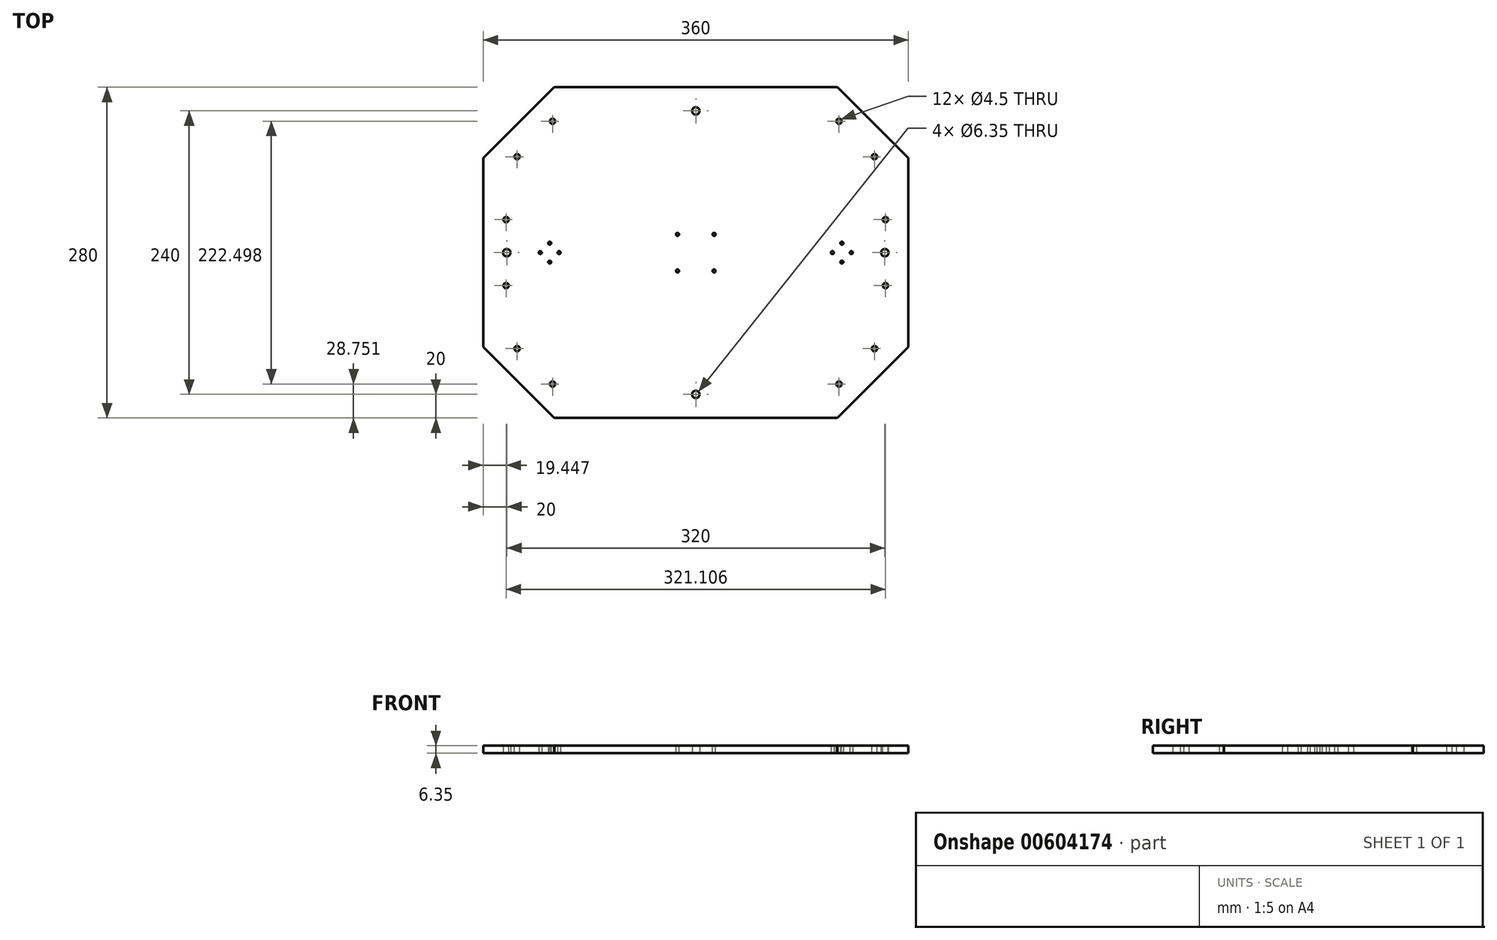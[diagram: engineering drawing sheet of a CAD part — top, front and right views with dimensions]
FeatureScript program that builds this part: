
annotation { "Feature Type Name" : "Feature", "Feature Type Description" : "" }
export const myFeature = defineFeature(function(context is Context, id is Id, definition is map)
    precondition{}
    {
        {
            var Q0;
            Q0=qCreatedBy(makeId("Top.planeOp"),FACE);
            var sketch = newSketch(context, id + "F0", { "sketchPlane" : qUnion([Q0])});
            skLineSegment(sketch, "E0", {"start": v(-120, 0) * mm, "end": v(-180, 60) * mm});
            skLineSegment(sketch, "E1", {"start": v(-180, 60) * mm, "end": v(-180, 220) * mm});
            skLineSegment(sketch, "E2", {"start": v(-180, 220) * mm, "end": v(-120, 280) * mm});
            skLineSegment(sketch, "E3", {"start": v(-120, 280) * mm, "end": v(120, 280) * mm});
            skLineSegment(sketch, "E4", {"start": v(120, 280) * mm, "end": v(180, 220) * mm});
            skLineSegment(sketch, "E5", {"start": v(180, 220) * mm, "end": v(180, 60) * mm});
            skLineSegment(sketch, "E6", {"start": v(180, 60) * mm, "end": v(120, 0) * mm});
            skLineSegment(sketch, "E7", {"start": v(120, 0) * mm, "end": v(-120, 0) * mm});
            skLineSegment(sketch, "E8", {"start": v(-180, 140) * mm, "end": v(-160, 140) * mm, "construction": true});
            skLineSegment(sketch, "E9", {"start": v(0, 280) * mm, "end": v(0, 260) * mm, "construction": true});
            skPoint(sketch, "E9.endSnap0", {"position": v(0, 280) * mm});
            skLineSegment(sketch, "E10", {"start": v(180, 140) * mm, "end": v(160, 140) * mm, "construction": true});
            skLineSegment(sketch, "E11", {"start": v(0, 0) * mm, "end": v(0, 20) * mm, "construction": true});
            skCircle(sketch, "E12", {"center": v(0, 20) * mm, "radius": 3.18 * mm});
            skCircle(sketch, "E13", {"center": v(160, 140) * mm, "radius": 3.18 * mm});
            skCircle(sketch, "E14", {"center": v(0, 260) * mm, "radius": 3.18 * mm});
            skCircle(sketch, "E15", {"center": v(-160, 140) * mm, "radius": 3.18 * mm});
            skLineSegment(sketch, "E16", {"start": v(-180, 140) * mm, "end": v(180, 140) * mm, "construction": true});
            skCircle(sketch, "E17", {"center": v(-123.65, 140) * mm, "radius": 8 * mm, "construction": true});
            skCircle(sketch, "E18", {"center": v(123.65, 140) * mm, "radius": 8 * mm, "construction": true});
            skPoint(sketch, "E19", {"position": v(-123.65, 148) * mm});
            skPoint(sketch, "E20", {"position": v(-123.65, 132) * mm});
            skPoint(sketch, "E21", {"position": v(-115.65, 140) * mm});
            skPoint(sketch, "E22", {"position": v(-131.65, 140) * mm});
            skPoint(sketch, "E23", {"position": v(131.65, 140) * mm});
            skPoint(sketch, "E24", {"position": v(115.65, 140) * mm});
            skPoint(sketch, "E25", {"position": v(123.65, 148) * mm});
            skPoint(sketch, "E26", {"position": v(123.65, 132) * mm});
            skPoint(sketch, "E27", {"position": v(0, 140) * mm});
            skSolve(sketch);
        }
        {
            var Q0;
            Q0=makeQuery(id+"F0.imprint","IMPRINT",FACE,{"disambiguationData":[TD([[makeQuery(id+"F0.imprint","IMPRINT",EDGE,{"derivedFrom":sQuery(id+"F0.wireOp",EDGE,"E0")}),-1.0]])]});
            extrude(context, id + "F1", {"entities" : qUnion([Q0]), "depth" : 6.35 * mm, "offsetDistance" : 25 * mm});
        }
        {
            var Q0;
            Q0=makeQuery(id+"F1.opExtrude","CAP_FACE",FACE,{"disambiguationData":[OSD([sQuery(id+"F0.wireOp",EDGE,"E0"),sQuery(id+"F0.wireOp",EDGE,"E1"),sQuery(id+"F0.wireOp",EDGE,"E2"),sQuery(id+"F0.wireOp",EDGE,"E3"),sQuery(id+"F0.wireOp",EDGE,"E4"),sQuery(id+"F0.wireOp",EDGE,"E5"),sQuery(id+"F0.wireOp",EDGE,"E6"),sQuery(id+"F0.wireOp",EDGE,"E7"),sQuery(id+"F0.wireOp",EDGE,"E12"),sQuery(id+"F0.wireOp",EDGE,"E13"),sQuery(id+"F0.wireOp",EDGE,"E14"),sQuery(id+"F0.wireOp",EDGE,"E15")])],"isStart":false});
            var sketch = newSketch(context, id + "F2", { "sketchPlane" : qUnion([Q0])});
            skLineSegment(sketch, "E28", {"start": v(-180, 140) * mm, "end": v(180, 140) * mm, "construction": true});
            skPoint(sketch, "E29", {"position": v(0, 140) * mm});
            skLineSegment(sketch, "E30.bottom", {"start": v(15.5, 155.5) * mm, "end": v(-15.5, 155.5) * mm, "construction": true});
            skLineSegment(sketch, "E30.top", {"start": v(15.5, 124.5) * mm, "end": v(-15.5, 124.5) * mm, "construction": true});
            skLineSegment(sketch, "E30.left", {"start": v(15.5, 155.5) * mm, "end": v(15.5, 124.5) * mm, "construction": true});
            skLineSegment(sketch, "E30.right", {"start": v(-15.5, 155.5) * mm, "end": v(-15.5, 124.5) * mm, "construction": true});
            skSolve(sketch);
        }
        {
            var Q0;
            Q0=sQuery(id+"F2.wireOp",VERTEX,"E30.bottom.end");
            var Q1;
            Q1=sQuery(id+"F2.wireOp",VERTEX,"E30.left.start");
            var Q2;
            Q2=sQuery(id+"F2.wireOp",VERTEX,"E30.top.start");
            var Q3;
            Q3=sQuery(id+"F2.wireOp",VERTEX,"E30.top.end");
            var Q4;
            Q4=makeQuery(id+"F1.opExtrude","SWEPT_BODY",BODY,{"disambiguationData":[OSD([sQuery(id+"F0.wireOp",EDGE,"E0"),sQuery(id+"F0.wireOp",EDGE,"E1"),sQuery(id+"F0.wireOp",EDGE,"E2"),sQuery(id+"F0.wireOp",EDGE,"E3"),sQuery(id+"F0.wireOp",EDGE,"E4"),sQuery(id+"F0.wireOp",EDGE,"E5"),sQuery(id+"F0.wireOp",EDGE,"E6"),sQuery(id+"F0.wireOp",EDGE,"E7"),sQuery(id+"F0.wireOp",EDGE,"E12"),sQuery(id+"F0.wireOp",EDGE,"E13"),sQuery(id+"F0.wireOp",EDGE,"E14"),sQuery(id+"F0.wireOp",EDGE,"E15")])]});
            hole(context, id + "F3", {"style" : HoleStyle.SIMPLE, "endStyle" : HoleEndStyle.BLIND, "standardTappedOrClearance" : lookupTablePath({ "standard" : "ANSI", "engagement" : "75%", "pitch" : "40 tpi", "size" : "#5", "type" : "Tapped" }), "standardBlindInLast" : lookupTablePath({ "standard" : "ANSI", "engagement" : "75%", "pitch" : "40 tpi", "size" : "#5", "type" : "Tapped" }), "holeDiameter" : 2.58 * mm, "majorDiameter" : 3.17 * mm, "showTappedDepth" : true, "holeDepth" : 13.9 * mm, "isTappedThrough" : true, "tappedDepth" : 12 * mm, "tapClearance" : 3, "locations" : qUnion([Q0, Q1, Q2, Q3]), "scope" : qUnion([Q4])});
        }
        {
            var Q0;
            Q0=makeQuery(id+"F1.opExtrude","CAP_FACE",FACE,{"disambiguationData":[OSD([sQuery(id+"F0.wireOp",EDGE,"E0"),sQuery(id+"F0.wireOp",EDGE,"E1"),sQuery(id+"F0.wireOp",EDGE,"E2"),sQuery(id+"F0.wireOp",EDGE,"E3"),sQuery(id+"F0.wireOp",EDGE,"E4"),sQuery(id+"F0.wireOp",EDGE,"E5"),sQuery(id+"F0.wireOp",EDGE,"E6"),sQuery(id+"F0.wireOp",EDGE,"E7"),sQuery(id+"F0.wireOp",EDGE,"E12"),sQuery(id+"F0.wireOp",EDGE,"E13"),sQuery(id+"F0.wireOp",EDGE,"E14"),sQuery(id+"F0.wireOp",EDGE,"E15")])],"isStart":false});
            var sketch = newSketch(context, id + "F4", { "sketchPlane" : qUnion([Q0])});
            skLineSegment(sketch, "E31", {"start": v(-180, 140) * mm, "end": v(-180, 167.94) * mm, "construction": true});
            skLineSegment(sketch, "E32", {"start": v(-180, 140) * mm, "end": v(-180, 112.06) * mm, "construction": true});
            skLineSegment(sketch, "E33", {"start": v(-180, 167.94) * mm, "end": v(-160.55, 167.94) * mm, "construction": true});
            skLineSegment(sketch, "E34", {"start": v(-180, 112.06) * mm, "end": v(-160.55, 112.06) * mm, "construction": true});
            skLineSegment(sketch, "E35", {"start": v(0, 280) * mm, "end": v(0, 0) * mm, "construction": true});
            skLineSegment(sketch, "E36.MirrorCS", {"start": v(180, 167.94) * mm, "end": v(160.55, 167.94) * mm, "construction": true});
            skLineSegment(sketch, "E37.MirrorCS", {"start": v(180, 112.06) * mm, "end": v(160.55, 112.06) * mm, "construction": true});
            skLineSegment(sketch, "E38", {"start": v(-120, 280) * mm, "end": v(-180, 220) * mm, "construction": true});
            skLineSegment(sketch, "E39", {"start": v(-180, 220) * mm, "end": v(-150, 250) * mm, "construction": true});
            skLineSegment(sketch, "E40", {"start": v(-150, 250) * mm, "end": v(-165, 235) * mm, "construction": true});
            skLineSegment(sketch, "E41", {"start": v(-165, 235) * mm, "end": v(-151.25, 221.25) * mm, "construction": true});
            skLineSegment(sketch, "E42", {"start": v(-150, 250) * mm, "end": v(-112, 212) * mm, "construction": true});
            skLineSegment(sketch, "E43.MirrorCS", {"start": v(-135, 265) * mm, "end": v(-121.25, 251.25) * mm, "construction": true});
            skLineSegment(sketch, "E44.MirrorCS", {"start": v(135, 265) * mm, "end": v(121.25, 251.25) * mm, "construction": true});
            skLineSegment(sketch, "E45.MirrorCS", {"start": v(165, 235) * mm, "end": v(151.25, 221.25) * mm, "construction": true});
            skLineSegment(sketch, "E46", {"start": v(-180, 60) * mm, "end": v(-120, 0) * mm, "construction": true});
            skLineSegment(sketch, "E47", {"start": v(-120, 0) * mm, "end": v(-150, 30) * mm, "construction": true});
            skLineSegment(sketch, "E48", {"start": v(-150, 30) * mm, "end": v(-135, 15) * mm, "construction": true});
            skLineSegment(sketch, "E49", {"start": v(-135, 15) * mm, "end": v(-121.25, 28.75) * mm, "construction": true});
            skLineSegment(sketch, "E50", {"start": v(-150, 30) * mm, "end": v(-108.05, 71.95) * mm, "construction": true});
            skLineSegment(sketch, "E51.MirrorCS", {"start": v(-165, 45) * mm, "end": v(-151.25, 58.75) * mm, "construction": true});
            skLineSegment(sketch, "E52.MirrorCS", {"start": v(165, 45) * mm, "end": v(151.25, 58.75) * mm, "construction": true});
            skLineSegment(sketch, "E53.MirrorCS", {"start": v(135, 15) * mm, "end": v(121.25, 28.75) * mm, "construction": true});
            skLineSegment(sketch, "E54", {"start": v(-151.25, 221.25) * mm, "end": v(-149.9, 222.6) * mm, "construction": true});
            skLineSegment(sketch, "E55", {"start": v(-121.25, 251.25) * mm, "end": v(-122.6, 249.9) * mm, "construction": true});
            skLineSegment(sketch, "E56", {"start": v(-121.25, 28.75) * mm, "end": v(-122.6, 30.1) * mm, "construction": true});
            skLineSegment(sketch, "E57", {"start": v(-151.25, 58.75) * mm, "end": v(-149.9, 57.4) * mm, "construction": true});
            skLineSegment(sketch, "E58.MirrorCS", {"start": v(121.25, 28.75) * mm, "end": v(122.6, 30.1) * mm, "construction": true});
            skLineSegment(sketch, "E59.MirrorCS", {"start": v(151.25, 58.75) * mm, "end": v(149.9, 57.4) * mm, "construction": true});
            skLineSegment(sketch, "E60.MirrorCS", {"start": v(151.25, 221.25) * mm, "end": v(149.9, 222.6) * mm, "construction": true});
            skLineSegment(sketch, "E61.MirrorCS", {"start": v(121.25, 251.25) * mm, "end": v(122.6, 249.9) * mm, "construction": true});
            skLineSegment(sketch, "E62", {"start": v(180, 140) * mm, "end": v(0, 140) * mm, "construction": true});
            skSolve(sketch);
        }
        {
            var Q0;
            Q0=sQuery(id+"F4.wireOp",VERTEX,"E33.end");
            var Q1;
            Q1=sQuery(id+"F4.wireOp",VERTEX,"E34.end");
            var Q2;
            Q2=sQuery(id+"F4.wireOp",VERTEX,"E37.MirrorCS.end");
            var Q3;
            Q3=sQuery(id+"F4.wireOp",VERTEX,"E36.MirrorCS.end");
            var Q4;
            Q4=makeQuery(id+"F1.opExtrude","SWEPT_BODY",BODY,{"disambiguationData":[OSD([sQuery(id+"F0.wireOp",EDGE,"E0"),sQuery(id+"F0.wireOp",EDGE,"E1"),sQuery(id+"F0.wireOp",EDGE,"E2"),sQuery(id+"F0.wireOp",EDGE,"E3"),sQuery(id+"F0.wireOp",EDGE,"E4"),sQuery(id+"F0.wireOp",EDGE,"E5"),sQuery(id+"F0.wireOp",EDGE,"E6"),sQuery(id+"F0.wireOp",EDGE,"E7"),sQuery(id+"F0.wireOp",EDGE,"E12"),sQuery(id+"F0.wireOp",EDGE,"E13"),sQuery(id+"F0.wireOp",EDGE,"E14"),sQuery(id+"F0.wireOp",EDGE,"E15")])]});
            hole(context, id + "F5", {"style" : HoleStyle.SIMPLE, "endStyle" : HoleEndStyle.THROUGH, "holeDiameter" : 4.5 * mm, "majorDiameter" : 5 * mm, "isTappedThrough" : true, "tappedDepth" : 12 * mm, "tapClearance" : 3, "locations" : qUnion([Q0, Q1, Q2, Q3]), "scope" : qUnion([Q4])});
        }
        {
            var Q0;
            Q0=sQuery(id+"F4.wireOp",VERTEX,"E54.start");
            var Q1;
            Q1=sQuery(id+"F4.wireOp",VERTEX,"E55.start");
            var Q2;
            Q2=makeQuery(id+"F1.opExtrude","SWEPT_BODY",BODY,{"disambiguationData":[OSD([sQuery(id+"F0.wireOp",EDGE,"E0"),sQuery(id+"F0.wireOp",EDGE,"E1"),sQuery(id+"F0.wireOp",EDGE,"E2"),sQuery(id+"F0.wireOp",EDGE,"E3"),sQuery(id+"F0.wireOp",EDGE,"E4"),sQuery(id+"F0.wireOp",EDGE,"E5"),sQuery(id+"F0.wireOp",EDGE,"E6"),sQuery(id+"F0.wireOp",EDGE,"E7"),sQuery(id+"F0.wireOp",EDGE,"E12"),sQuery(id+"F0.wireOp",EDGE,"E13"),sQuery(id+"F0.wireOp",EDGE,"E14"),sQuery(id+"F0.wireOp",EDGE,"E15")])]});
            hole(context, id + "F6", {"style" : HoleStyle.SIMPLE, "endStyle" : HoleEndStyle.BLIND, "holeDiameter" : 4.5 * mm, "majorDiameter" : 5 * mm, "holeDepth" : 12 * mm, "isTappedThrough" : true, "tappedDepth" : 12 * mm, "tapClearance" : 3, "locations" : qUnion([Q0, Q1]), "scope" : qUnion([Q2])});
        }
        {
            var Q0;
            Q0=sQuery(id+"F4.wireOp",VERTEX,"E61.MirrorCS.start");
            var Q1;
            Q1=sQuery(id+"F4.wireOp",VERTEX,"E60.MirrorCS.start");
            var Q2;
            Q2=sQuery(id+"F4.wireOp",VERTEX,"E57.start");
            var Q3;
            Q3=sQuery(id+"F4.wireOp",VERTEX,"E49.end");
            var Q4;
            Q4=sQuery(id+"F4.wireOp",VERTEX,"E53.MirrorCS.end");
            var Q5;
            Q5=sQuery(id+"F4.wireOp",VERTEX,"E59.MirrorCS.start");
            var Q6;
            Q6=makeQuery(id+"F1.opExtrude","SWEPT_BODY",BODY,{"disambiguationData":[OSD([sQuery(id+"F0.wireOp",EDGE,"E0"),sQuery(id+"F0.wireOp",EDGE,"E1"),sQuery(id+"F0.wireOp",EDGE,"E2"),sQuery(id+"F0.wireOp",EDGE,"E3"),sQuery(id+"F0.wireOp",EDGE,"E4"),sQuery(id+"F0.wireOp",EDGE,"E5"),sQuery(id+"F0.wireOp",EDGE,"E6"),sQuery(id+"F0.wireOp",EDGE,"E7"),sQuery(id+"F0.wireOp",EDGE,"E12"),sQuery(id+"F0.wireOp",EDGE,"E13"),sQuery(id+"F0.wireOp",EDGE,"E14"),sQuery(id+"F0.wireOp",EDGE,"E15")])]});
            hole(context, id + "F7", {"style" : HoleStyle.SIMPLE, "endStyle" : HoleEndStyle.BLIND, "holeDiameter" : 4.5 * mm, "majorDiameter" : 5 * mm, "holeDepth" : 12 * mm, "isTappedThrough" : true, "tappedDepth" : 12 * mm, "tapClearance" : 3, "locations" : qUnion([Q0, Q1, Q2, Q3, Q4, Q5]), "scope" : qUnion([Q6])});
        }
        {
            var Q0;
            Q0=sQuery(id+"F0.wireOp",VERTEX,"E19");
            var Q1;
            Q1=sQuery(id+"F0.wireOp",VERTEX,"E21");
            var Q2;
            Q2=sQuery(id+"F0.wireOp",VERTEX,"E20");
            var Q3;
            Q3=sQuery(id+"F0.wireOp",VERTEX,"E22");
            var Q4;
            Q4=sQuery(id+"F0.wireOp",VERTEX,"E25");
            var Q5;
            Q5=sQuery(id+"F0.wireOp",VERTEX,"E23");
            var Q6;
            Q6=sQuery(id+"F0.wireOp",VERTEX,"E24");
            var Q7;
            Q7=sQuery(id+"F0.wireOp",VERTEX,"E26");
            var Q8;
            Q8=makeQuery(id+"F1.opExtrude","SWEPT_BODY",BODY,{"disambiguationData":[OSD([sQuery(id+"F0.wireOp",EDGE,"E0"),sQuery(id+"F0.wireOp",EDGE,"E1"),sQuery(id+"F0.wireOp",EDGE,"E2"),sQuery(id+"F0.wireOp",EDGE,"E3"),sQuery(id+"F0.wireOp",EDGE,"E4"),sQuery(id+"F0.wireOp",EDGE,"E5"),sQuery(id+"F0.wireOp",EDGE,"E6"),sQuery(id+"F0.wireOp",EDGE,"E7"),sQuery(id+"F0.wireOp",EDGE,"E12"),sQuery(id+"F0.wireOp",EDGE,"E13"),sQuery(id+"F0.wireOp",EDGE,"E14"),sQuery(id+"F0.wireOp",EDGE,"E15")])]});
            hole(context, id + "F8", {"style" : HoleStyle.SIMPLE, "endStyle" : HoleEndStyle.THROUGH, "oppositeDirection" : true, "standardTappedOrClearance" : lookupTablePath({ "standard" : "ISO", "engagement" : "75%", "pitch" : "0.5 mm", "size" : "M3", "type" : "Tapped" }), "standardBlindInLast" : lookupTablePath({ "standard" : "ISO", "engagement" : "75%", "pitch" : "0.5 mm", "size" : "M3", "type" : "Tapped" }), "holeDiameter" : 2.5 * mm, "majorDiameter" : 3 * mm, "showTappedDepth" : true, "isTappedThrough" : true, "tappedDepth" : 12 * mm, "tapClearance" : 3, "locations" : qUnion([Q0, Q1, Q2, Q3, Q4, Q5, Q6, Q7]), "scope" : qUnion([Q8])});
        }
    });
